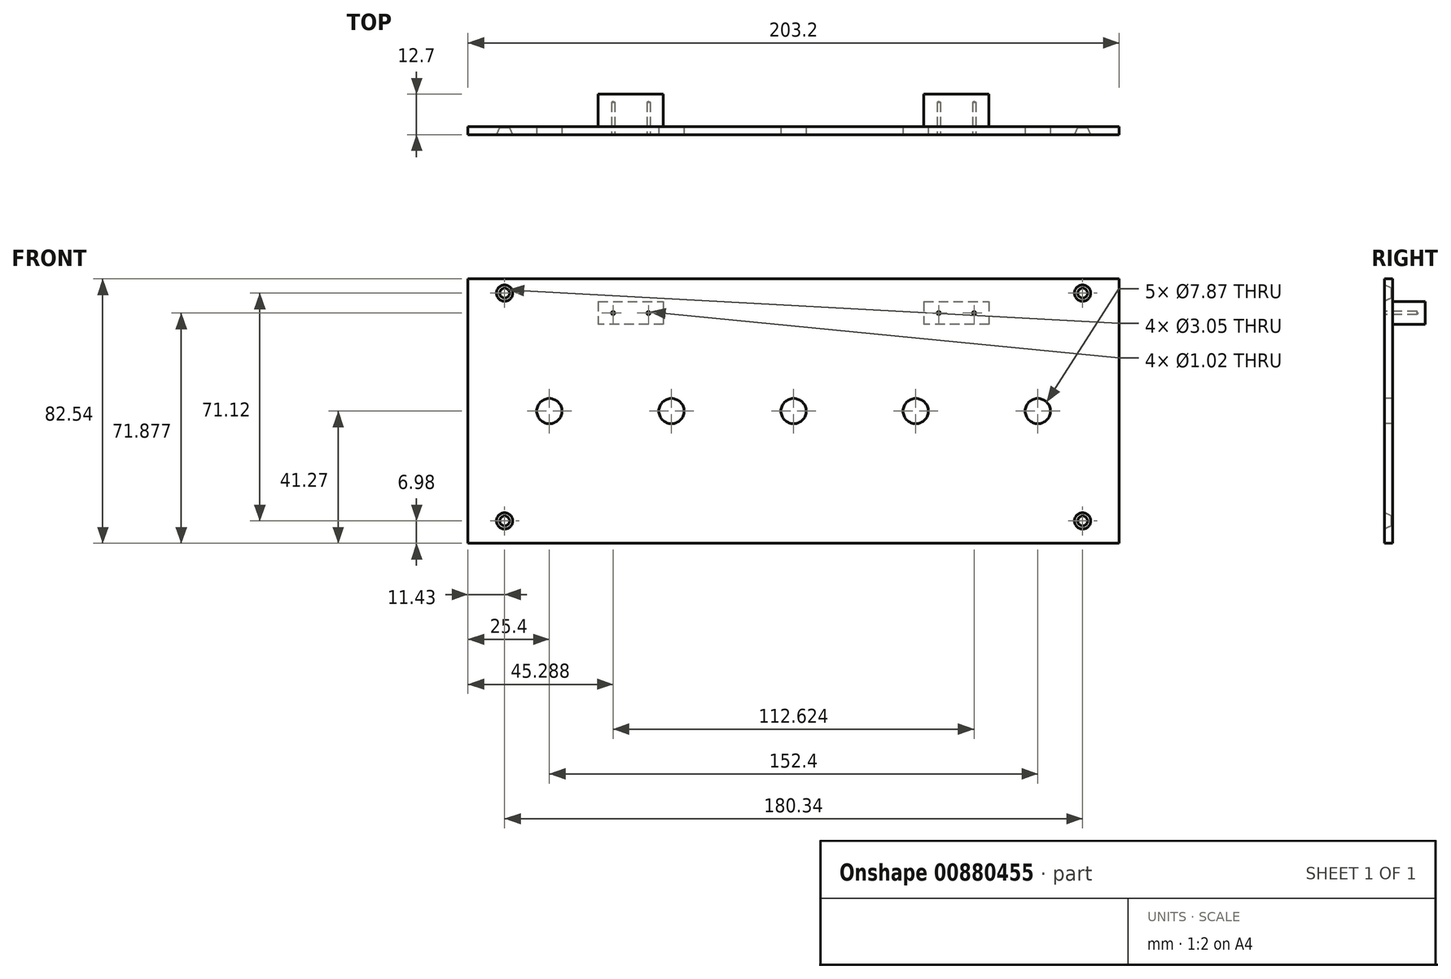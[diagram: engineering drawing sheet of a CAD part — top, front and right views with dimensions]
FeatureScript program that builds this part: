
annotation { "Feature Type Name" : "Feature", "Feature Type Description" : "" }
export const myFeature = defineFeature(function(context is Context, id is Id, definition is map)
    precondition{}
    {
        {
            var Q0;
            Q0=qCreatedBy(makeId("Front.planeOp"),FACE);
            var sketch = newSketch(context, id + "F0", { "sketchPlane" : qUnion([Q0])});
            skLineSegment(sketch, "E0.bottom", {"start": v(-101.6, 41.27) * mm, "end": v(101.6, 41.27) * mm});
            skLineSegment(sketch, "E0.top", {"start": v(-101.6, -41.27) * mm, "end": v(101.6, -41.27) * mm});
            skLineSegment(sketch, "E0.left", {"start": v(-101.6, 41.27) * mm, "end": v(-101.6, -41.27) * mm});
            skLineSegment(sketch, "E0.right", {"start": v(101.6, 41.27) * mm, "end": v(101.6, -41.27) * mm});
            skPoint(sketch, "E0.middle", {"position": v(0, 0) * mm});
            skSolve(sketch);
        }
        {
            var Q0;
            Q0=qSketchRegion(id+"F0",true);
            extrude(context, id + "F1", {"entities" : qUnion([Q0]), "depth" : 2.54 * mm, "offsetDistance" : 25.4 * mm});
        }
        {
            var Q0;
            Q0=makeQuery(id+"F1.opExtrude","CAP_FACE",FACE,{"disambiguationData":[OSD([sQuery(id+"F0.wireOp",EDGE,"E0.bottom"),sQuery(id+"F0.wireOp",EDGE,"E0.top"),sQuery(id+"F0.wireOp",EDGE,"E0.left"),sQuery(id+"F0.wireOp",EDGE,"E0.right")])],"isStart":false});
            var sketch = newSketch(context, id + "F2", { "sketchPlane" : qUnion([Q0])});
            skLineSegment(sketch, "E1", {"start": v(-101.6, 0) * mm, "end": v(101.6, 0) * mm, "construction": true});
            skPoint(sketch, "E2", {"position": v(0, 0) * mm});
            skPoint(sketch, "E3", {"position": v(-38.1, 0) * mm});
            skPoint(sketch, "E4", {"position": v(-76.2, 0) * mm});
            skPoint(sketch, "E5", {"position": v(38.1, 0) * mm});
            skPoint(sketch, "E6", {"position": v(76.2, 0) * mm});
            skLineSegment(sketch, "E7", {"start": v(0, 41.27) * mm, "end": v(-50.8, 41.27) * mm});
            skLineSegment(sketch, "E8", {"start": v(0, 41.27) * mm, "end": v(50.8, 41.27) * mm});
            skLineSegment(sketch, "E9.bottom", {"start": v(-60.96, 37.21) * mm, "end": v(-40.64, 37.21) * mm});
            skLineSegment(sketch, "E9.top", {"start": v(-60.96, 45.34) * mm, "end": v(-40.64, 45.34) * mm});
            skLineSegment(sketch, "E9.left", {"start": v(-60.96, 37.21) * mm, "end": v(-60.96, 45.34) * mm});
            skLineSegment(sketch, "E9.right", {"start": v(-40.64, 37.21) * mm, "end": v(-40.64, 45.34) * mm});
            skPoint(sketch, "E9.middle", {"position": v(-50.8, 41.27) * mm});
            skLineSegment(sketch, "E10.bottom", {"start": v(40.64, 37.21) * mm, "end": v(60.96, 37.21) * mm});
            skLineSegment(sketch, "E10.top", {"start": v(40.64, 45.34) * mm, "end": v(60.96, 45.34) * mm});
            skLineSegment(sketch, "E10.left", {"start": v(40.64, 37.21) * mm, "end": v(40.64, 45.34) * mm});
            skLineSegment(sketch, "E10.right", {"start": v(60.96, 37.21) * mm, "end": v(60.96, 45.34) * mm});
            skPoint(sketch, "E10.middle", {"position": v(50.8, 41.27) * mm});
            skLineSegment(sketch, "E11.bottom", {"start": v(-40.64, 37.21) * mm, "end": v(-60.96, 37.21) * mm});
            skLineSegment(sketch, "E11.top", {"start": v(-40.64, 37.21) * mm, "end": v(-60.96, 37.21) * mm});
            skLineSegment(sketch, "E11.left", {"start": v(-40.64, 37.21) * mm, "end": v(-40.64, 37.21) * mm});
            skLineSegment(sketch, "E11.right", {"start": v(-60.96, 37.21) * mm, "end": v(-60.96, 37.21) * mm});
            skLineSegment(sketch, "E12.top", {"start": v(-40.64, 27.05) * mm, "end": v(-60.96, 27.05) * mm});
            skLineSegment(sketch, "E12.left", {"start": v(-40.64, 37.21) * mm, "end": v(-40.64, 27.05) * mm});
            skLineSegment(sketch, "E12.right", {"start": v(-60.96, 37.21) * mm, "end": v(-60.96, 27.05) * mm});
            skLineSegment(sketch, "E13.bottom", {"start": v(60.96, 37.21) * mm, "end": v(40.64, 37.21) * mm});
            skLineSegment(sketch, "E13.top", {"start": v(60.96, 27.05) * mm, "end": v(40.64, 27.05) * mm});
            skLineSegment(sketch, "E13.left", {"start": v(60.96, 37.21) * mm, "end": v(60.96, 27.05) * mm});
            skLineSegment(sketch, "E13.right", {"start": v(40.64, 37.21) * mm, "end": v(40.64, 27.05) * mm});
            skLineSegment(sketch, "E14.bottom", {"start": v(-99.06, 41.27) * mm, "end": v(-82.55, 41.27) * mm, "construction": true});
            skLineSegment(sketch, "E14.top", {"start": v(-99.06, 32.38) * mm, "end": v(-82.55, 32.38) * mm, "construction": true});
            skLineSegment(sketch, "E14.left", {"start": v(-99.06, 41.27) * mm, "end": v(-99.06, 32.38) * mm, "construction": true});
            skLineSegment(sketch, "E14.right", {"start": v(-82.55, 41.27) * mm, "end": v(-82.55, 32.38) * mm, "construction": true});
            skLineSegment(sketch, "E15.bottom", {"start": v(99.06, 41.27) * mm, "end": v(82.55, 41.27) * mm, "construction": true});
            skLineSegment(sketch, "E15.top", {"start": v(99.06, 32.38) * mm, "end": v(82.55, 32.38) * mm, "construction": true});
            skLineSegment(sketch, "E15.left", {"start": v(99.06, 41.27) * mm, "end": v(99.06, 32.39) * mm, "construction": true});
            skLineSegment(sketch, "E15.right", {"start": v(82.55, 41.27) * mm, "end": v(82.55, 32.38) * mm, "construction": true});
            skLineSegment(sketch, "E16.bottom", {"start": v(99.06, -29.85) * mm, "end": v(82.55, -29.85) * mm, "construction": true});
            skLineSegment(sketch, "E16.top", {"start": v(99.06, -38.73) * mm, "end": v(82.55, -38.73) * mm, "construction": true});
            skLineSegment(sketch, "E16.left", {"start": v(99.06, -29.85) * mm, "end": v(99.06, -38.73) * mm, "construction": true});
            skLineSegment(sketch, "E16.right", {"start": v(82.55, -29.85) * mm, "end": v(82.55, -38.73) * mm, "construction": true});
            skLineSegment(sketch, "E17.bottom", {"start": v(-99.06, -38.73) * mm, "end": v(-82.55, -38.73) * mm, "construction": true});
            skLineSegment(sketch, "E17.top", {"start": v(-99.06, -29.85) * mm, "end": v(-82.55, -29.85) * mm, "construction": true});
            skLineSegment(sketch, "E17.left", {"start": v(-99.06, -38.73) * mm, "end": v(-99.06, -29.85) * mm, "construction": true});
            skLineSegment(sketch, "E17.right", {"start": v(-82.55, -38.73) * mm, "end": v(-82.55, -29.85) * mm, "construction": true});
            skPoint(sketch, "E18", {"position": v(-90.17, 36.83) * mm});
            skPoint(sketch, "E18.positionSnap0", {"position": v(-82.55, 36.83) * mm});
            skPoint(sketch, "E19", {"position": v(-90.17, -34.3) * mm});
            skPoint(sketch, "E19.positionSnap0", {"position": v(-82.55, -34.3) * mm});
            skPoint(sketch, "E20", {"position": v(90.17, 36.83) * mm});
            skPoint(sketch, "E20.positionSnap0", {"position": v(82.55, 36.83) * mm});
            skPoint(sketch, "E21", {"position": v(90.17, -34.3) * mm});
            skPoint(sketch, "E21.positionSnap0", {"position": v(82.55, -34.3) * mm});
            skLineSegment(sketch, "E22", {"start": v(-60.96, 30.6) * mm, "end": v(-40.64, 30.6) * mm, "construction": true});
            skLineSegment(sketch, "E23", {"start": v(-40.64, 30.6) * mm, "end": v(40.64, 30.6) * mm, "construction": true});
            skLineSegment(sketch, "E24", {"start": v(40.64, 30.6) * mm, "end": v(60.96, 30.6) * mm, "construction": true});
            skPoint(sketch, "E25", {"position": v(-50.8, 30.6) * mm});
            skPoint(sketch, "E26", {"position": v(-56.31, 30.6) * mm});
            skPoint(sketch, "E27", {"position": v(-45.29, 30.6) * mm});
            skPoint(sketch, "E28", {"position": v(50.8, 30.6) * mm});
            skPoint(sketch, "E29", {"position": v(45.29, 30.6) * mm});
            skPoint(sketch, "E30", {"position": v(56.31, 30.6) * mm});
            skLineSegment(sketch, "E31", {"start": v(-60.96, 34.16) * mm, "end": v(-40.64, 34.16) * mm});
            skLineSegment(sketch, "E32", {"start": v(40.64, 34.16) * mm, "end": v(60.96, 34.16) * mm});
            skSolve(sketch);
        }
        {
            var Q0;
            Q0=sQuery(id+"F2.wireOp",VERTEX,"E4");
            var Q1;
            Q1=sQuery(id+"F2.wireOp",VERTEX,"E3");
            var Q2;
            Q2=sQuery(id+"F2.wireOp",VERTEX,"E2");
            var Q3;
            Q3=sQuery(id+"F2.wireOp",VERTEX,"E5");
            var Q4;
            Q4=sQuery(id+"F2.wireOp",VERTEX,"E6");
            var Q5;
            Q5=makeQuery(id+"F1.opExtrude","SWEPT_BODY",BODY,{"disambiguationData":[OSD([sQuery(id+"F0.wireOp",EDGE,"E0.bottom"),sQuery(id+"F0.wireOp",EDGE,"E0.top"),sQuery(id+"F0.wireOp",EDGE,"E0.left"),sQuery(id+"F0.wireOp",EDGE,"E0.right")])]});
            hole(context, id + "F3", {"style" : HoleStyle.SIMPLE, "endStyle" : HoleEndStyle.THROUGH, "holeDiameter" : 7.87 * mm, "majorDiameter" : 6.35 * mm, "isTappedThrough" : true, "tappedDepth" : 12.7 * mm, "tapClearance" : 3, "locations" : qUnion([Q0, Q1, Q2, Q3, Q4]), "scope" : qUnion([Q5])});
        }
        {
            var Q0;
            {var subQ1=sQuery(id+"F2.wireOp",EDGE,"E9.top");Q0=makeQuery(id+"F2.imprint","IMPRINT",FACE,{"disambiguationData":[TD([[makeQuery(id+"F2.imprint","IMPRINT",EDGE,{"derivedFrom":subQ1}),-1.0]])]});}
            var Q1;
            {var subQ1=sQuery(id+"F2.wireOp",EDGE,"E10.top");Q1=makeQuery(id+"F2.imprint","IMPRINT",FACE,{"disambiguationData":[TD([[makeQuery(id+"F2.imprint","IMPRINT",EDGE,{"derivedFrom":subQ1}),-1.0]])]});}
            var Q2;
            {var subQ0=sQuery(id+"F2.wireOp",EDGE,"E11.bottom");Q2=makeQuery(id+"F2.imprint","IMPRINT",FACE,{"disambiguationData":[TD([[makeQuery(id+"F2.imprint","IMPRINT",EDGE,{"derivedFrom":subQ0}),-1.0]])]});}
            var Q3;
            {var subQ0=sQuery(id+"F2.wireOp",EDGE,"E13.bottom");Q3=makeQuery(id+"F2.imprint","IMPRINT",FACE,{"disambiguationData":[TD([[makeQuery(id+"F2.imprint","IMPRINT",EDGE,{"derivedFrom":subQ0}),-1.0]])]});}
            extrude(context, id + "F4", {"entities" : qUnion([Q0, Q1, Q2, Q3]), "operationType" : NewBodyOperationType.REMOVE, "oppositeDirection" : true, "depth" : 25.4 * mm, "offsetDistance" : 25.4 * mm});
        }
        {
            var Q0;
            {var subQ0=sQuery(id+"F2.wireOp",EDGE,"E12.top");Q0=makeQuery(id+"F2.imprint","IMPRINT",FACE,{"disambiguationData":[TD([[makeQuery(id+"F2.imprint","IMPRINT",EDGE,{"derivedFrom":subQ0}),-1.0]])]});}
            var Q1;
            {var subQ0=sQuery(id+"F2.wireOp",EDGE,"E13.top");Q1=makeQuery(id+"F2.imprint","IMPRINT",FACE,{"disambiguationData":[TD([[makeQuery(id+"F2.imprint","IMPRINT",EDGE,{"derivedFrom":subQ0}),-1.0]])]});}
            extrude(context, id + "F5", {"entities" : qUnion([Q0, Q1]), "operationType" : NewBodyOperationType.ADD, "oppositeDirection" : true, "depth" : 12.7 * mm, "offsetDistance" : 25.4 * mm});
        }
        {
            var Q0;
            Q0=sQuery(id+"F2.wireOp",VERTEX,"E18");
            var Q1;
            Q1=sQuery(id+"F2.wireOp",VERTEX,"E19");
            var Q2;
            Q2=sQuery(id+"F2.wireOp",VERTEX,"E20");
            var Q3;
            Q3=sQuery(id+"F2.wireOp",VERTEX,"E21");
            var Q4;
            Q4=makeQuery(id+"F1.opExtrude","SWEPT_BODY",BODY,{"disambiguationData":[OSD([sQuery(id+"F0.wireOp",EDGE,"E0.bottom"),sQuery(id+"F0.wireOp",EDGE,"E0.top"),sQuery(id+"F0.wireOp",EDGE,"E0.left"),sQuery(id+"F0.wireOp",EDGE,"E0.right")])]});
            hole(context, id + "F6", {"style" : HoleStyle.C_SINK, "endStyle" : HoleEndStyle.THROUGH, "holeDiameter" : 3.05 * mm, "cSinkDiameter" : 5.08 * mm, "cSinkAngle" : 49 * degree, "majorDiameter" : 6.35 * mm, "isTappedThrough" : true, "tappedDepth" : 12.7 * mm, "tapClearance" : 3, "locations" : qUnion([Q0, Q1, Q2, Q3]), "scope" : qUnion([Q4])});
        }
        {
            var Q0;
            Q0=sQuery(id+"F2.wireOp",VERTEX,"E26");
            var Q1;
            Q1=sQuery(id+"F2.wireOp",VERTEX,"E27");
            var Q2;
            Q2=sQuery(id+"F2.wireOp",VERTEX,"E29");
            var Q3;
            Q3=sQuery(id+"F2.wireOp",VERTEX,"E30");
            var Q4;
            Q4=makeQuery(id+"F1.opExtrude","SWEPT_BODY",BODY,{"disambiguationData":[OSD([sQuery(id+"F0.wireOp",EDGE,"E0.bottom"),sQuery(id+"F0.wireOp",EDGE,"E0.top"),sQuery(id+"F0.wireOp",EDGE,"E0.left"),sQuery(id+"F0.wireOp",EDGE,"E0.right")])]});
            hole(context, id + "F7", {"style" : HoleStyle.SIMPLE, "endStyle" : HoleEndStyle.BLIND, "holeDiameter" : 1.02 * mm, "majorDiameter" : 6.35 * mm, "holeDepth" : 10.16 * mm, "isTappedThrough" : true, "tappedDepth" : 12.7 * mm, "tapClearance" : 3, "locations" : qUnion([Q0, Q1, Q2, Q3]), "scope" : qUnion([Q4])});
        }
    });
